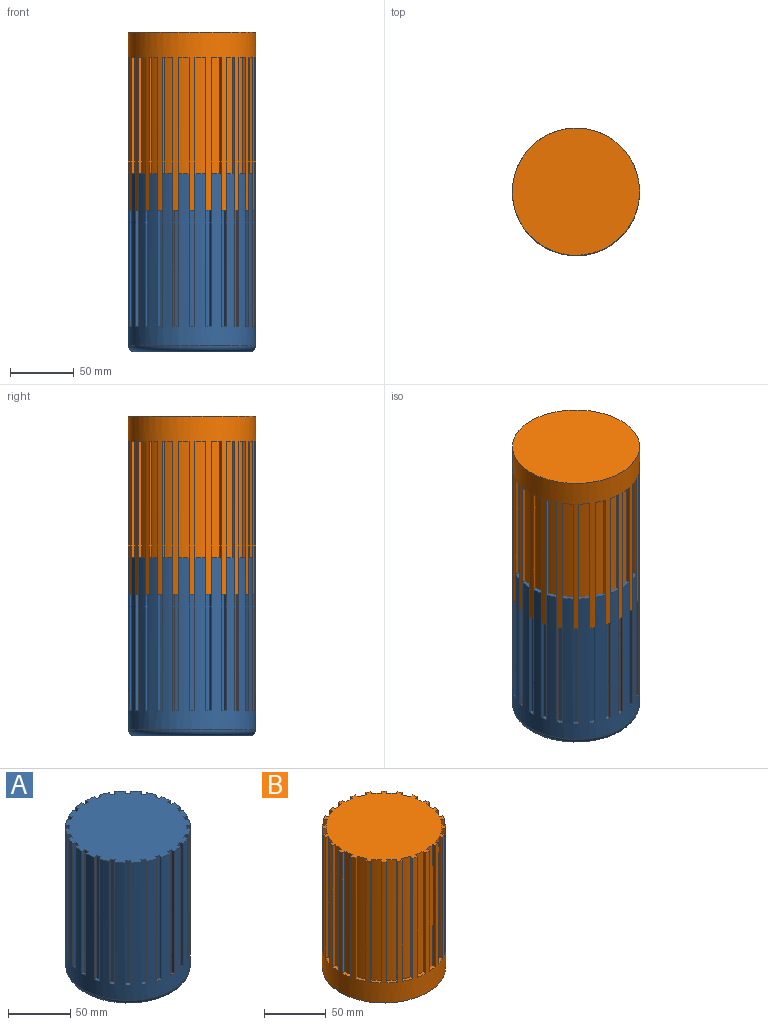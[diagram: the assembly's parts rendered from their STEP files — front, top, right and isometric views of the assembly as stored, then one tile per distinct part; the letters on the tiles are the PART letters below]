
ASSEMBLY  parts=2 mates=1
PART A: 102 faces, bbox 108.2x108.2x140 mm
  f0: plane 120x2.82mm, normal (0.94,0.34,0), area 360mm2, adj f1,f69,f70,f97
  f1: plane 120x3.86mm, normal (-0.26,0.97,0), area 480mm2, adj f0,f2,f70,f97
  f2: plane 120x2.95mm, normal (-0.98,-0.17,0), area 360mm2, adj f1,f69,f70,f97
  f3: plane 120x2.46mm, normal (0.82,0.57,0), area 360mm2, adj f4,f69,f70,f96
  f4: plane 120x3.46mm, normal (-0.5,0.87,0), area 480mm2, adj f3,f5,f70,f96
  f5: plane 120x2.72mm, normal (-0.91,-0.42,0), area 360mm2, adj f4,f69,f70,f96
  f6: plane 120x2.3mm, normal (0.64,0.77,0), area 360mm2, adj f7,f69,f70,f95
  f7: plane 120x2.83mm, normal (-0.71,0.71,0), area 480mm2, adj f6,f8,f70,f95
  f8: plane 120x2.3mm, normal (-0.77,-0.64,0), area 360mm2, adj f7,f69,f70,f95
  f9: plane 120x2.72mm, normal (0.42,0.91,0), area 360mm2, adj f10,f69,f70,f94
  f10: plane 120x3.46mm, normal (-0.87,0.5,0), area 480mm2, adj f9,f11,f70,f94
  f11: plane 120x2.46mm, normal (-0.57,-0.82,0), area 360mm2, adj f10,f69,f70,f94
  f12: plane 120x2.95mm, normal (0.17,0.98,0), area 360mm2, adj f13,f69,f70,f93
  f13: plane 120x3.86mm, normal (-0.97,0.26,0), area 480mm2, adj f12,f14,f70,f93
  f14: plane 120x2.82mm, normal (-0.34,-0.94,0), area 360mm2, adj f13,f69,f70,f93
  f15: plane 120x2.99mm, normal (-0.09,1,0), area 360mm2, adj f16,f69,f70,f92
  f16: plane 120x4mm, normal (-1,0,0), area 480mm2, adj f15,f17,f70,f92
  f17: plane 120x2.99mm, normal (-0.09,-1,0), area 360mm2, adj f16,f69,f70,f92
  f18: plane 120x2.82mm, normal (-0.34,0.94,0), area 360mm2, adj f19,f69,f70,f91
  f19: plane 120x3.86mm, normal (-0.97,-0.26,0), area 480mm2, adj f18,f20,f70,f91
  f20: plane 120x2.95mm, normal (0.17,-0.98,0), area 360mm2, adj f19,f69,f70,f91
  f21: plane 120x2.46mm, normal (-0.57,0.82,0), area 360mm2, adj f22,f69,f70,f90
  f22: plane 120x3.46mm, normal (-0.87,-0.5,0), area 480mm2, adj f21,f23,f70,f90
  f23: plane 120x2.72mm, normal (0.42,-0.91,0), area 360mm2, adj f22,f69,f70,f90
  f24: plane 120x2.3mm, normal (-0.77,0.64,0), area 360mm2, adj f25,f69,f70,f89
  f25: plane 120x2.83mm, normal (-0.71,-0.71,0), area 480mm2, adj f24,f26,f70,f89
  f26: plane 120x2.3mm, normal (0.64,-0.77,0), area 360mm2, adj f25,f69,f70,f89
  f27: plane 120x2.72mm, normal (-0.91,0.42,0), area 360mm2, adj f28,f69,f70,f88
  f28: plane 120x3.46mm, normal (-0.5,-0.87,0), area 480mm2, adj f27,f29,f70,f88
  f29: plane 120x2.46mm, normal (0.82,-0.57,0), area 360mm2, adj f28,f69,f70,f88
  f30: plane 120x2.95mm, normal (-0.98,0.17,0), area 360mm2, adj f31,f69,f70,f87
  f31: plane 120x3.86mm, normal (-0.26,-0.97,0), area 480mm2, adj f30,f32,f70,f87
  f32: plane 120x2.82mm, normal (0.94,-0.34,0), area 360mm2, adj f31,f69,f70,f87
  f33: plane 120x2.99mm, normal (-1,-0.09,0), area 360mm2, adj f34,f69,f70,f86
  f34: plane 120x4mm, normal (0,-1,0), area 480mm2, adj f33,f35,f70,f86
  f35: plane 120x2.99mm, normal (1,-0.09,0), area 360mm2, adj f34,f69,f70,f86
  f36: plane 120x2.82mm, normal (-0.94,-0.34,0), area 360mm2, adj f37,f69,f70,f85
  f37: plane 120x3.86mm, normal (0.26,-0.97,0), area 480mm2, adj f36,f38,f70,f85
  f38: plane 120x2.95mm, normal (0.98,0.17,0), area 360mm2, adj f37,f69,f70,f85
  f39: plane 120x2.46mm, normal (-0.82,-0.57,0), area 360mm2, adj f40,f69,f70,f84
  f40: plane 120x3.46mm, normal (0.5,-0.87,0), area 480mm2, adj f39,f41,f70,f84
  f41: plane 120x2.72mm, normal (0.91,0.42,0), area 360mm2, adj f40,f69,f70,f84
  f42: plane 120x2.3mm, normal (-0.64,-0.77,0), area 360mm2, adj f43,f69,f70,f83
  f43: plane 120x2.83mm, normal (0.71,-0.71,0), area 480mm2, adj f42,f44,f70,f83
  f44: plane 120x2.3mm, normal (0.77,0.64,0), area 360mm2, adj f43,f69,f70,f83
  f45: plane 120x2.72mm, normal (-0.42,-0.91,0), area 360mm2, adj f46,f69,f70,f82
  f46: plane 120x3.46mm, normal (0.87,-0.5,0), area 480mm2, adj f45,f47,f70,f82
  f47: plane 120x2.46mm, normal (0.57,0.82,0), area 360mm2, adj f46,f69,f70,f82
  f48: plane 120x2.95mm, normal (-0.17,-0.98,0), area 360mm2, adj f49,f69,f70,f81
  f49: plane 120x3.86mm, normal (0.97,-0.26,0), area 480mm2, adj f48,f50,f70,f81
  f50: plane 120x2.82mm, normal (0.34,0.94,0), area 360mm2, adj f49,f69,f70,f81
  f51: plane 120x2.99mm, normal (0.09,-1,0), area 360mm2, adj f52,f69,f70,f80
  f52: plane 120x4mm, normal (1,0,0), area 480mm2, adj f51,f53,f70,f80
  f53: plane 120x2.99mm, normal (0.09,1,0), area 360mm2, adj f52,f69,f70,f80
  f54: plane 120x2.82mm, normal (0.34,-0.94,0), area 360mm2, adj f55,f69,f70,f79
  f55: plane 120x3.86mm, normal (0.97,0.26,0), area 480mm2, adj f54,f56,f70,f79
  f56: plane 120x2.95mm, normal (-0.17,0.98,0), area 360mm2, adj f55,f69,f70,f79
  f57: plane 120x2.46mm, normal (0.57,-0.82,0), area 360mm2, adj f58,f69,f70,f78
  f58: plane 120x3.46mm, normal (0.87,0.5,0), area 480mm2, adj f57,f59,f70,f78
  f59: plane 120x2.72mm, normal (-0.42,0.91,0), area 360mm2, adj f58,f69,f70,f78
  f60: plane 120x2.3mm, normal (0.77,-0.64,0), area 360mm2, adj f61,f69,f70,f77
  f61: plane 120x2.83mm, normal (0.71,0.71,0), area 480mm2, adj f60,f62,f70,f77
  f62: plane 120x2.3mm, normal (-0.64,0.77,0), area 360mm2, adj f61,f69,f70,f77
  f63: plane 120x2.72mm, normal (0.91,-0.42,0), area 360mm2, adj f64,f69,f70,f76
  f64: plane 120x3.46mm, normal (0.5,0.87,0), area 480mm2, adj f63,f65,f70,f76
  f65: plane 120x2.46mm, normal (-0.82,0.57,0), area 360mm2, adj f64,f69,f70,f76
  f66: plane 120x2.95mm, normal (0.98,-0.17,0), area 360mm2, adj f67,f69,f70,f75
  f67: plane 120x3.86mm, normal (0.26,0.97,0), area 480mm2, adj f66,f68,f70,f75
  f68: plane 120x2.82mm, normal (-0.94,0.34,0), area 360mm2, adj f67,f69,f70,f75
  f69: cylinder r=50mm len=135mm, axis (0,0,-1), area 29313.1mm2, adj f0,f2,f3,f5,f6,f8,f9,f11
  f70: plane 99.9x99.9mm, normal (0,0,1), area 7544.6mm2, adj f0,f1,f2,f3,f4,f5,f6,f7
  f71: plane 120x4mm, normal (0,1,0), area 480mm2, adj f70,f72,f73,f74
  f72: plane 120x2.99mm, normal (-1,0.09,0), area 360mm2, adj f69,f70,f71,f74
  f73: plane 120x2.99mm, normal (1,0.09,0), area 360mm2, adj f69,f70,f71,f74
  f74: plane 4.52x3.04mm, normal (0,0,1), area 12.9mm2, adj f69,f71,f72,f73
  f75: plane 4.89x3.99mm, normal (0,0,1), area 12.9mm2, adj f66,f67,f68,f69
  f76: plane 5.19x4.72mm, normal (0,0,1), area 12.9mm2, adj f63,f64,f65,f69
  f77: plane 5.13x5.13mm, normal (0,0,1), area 12.9mm2, adj f60,f61,f62,f69
  f78: plane 5.19x4.72mm, normal (0,0,1), area 12.9mm2, adj f57,f58,f59,f69
  f79: plane 4.89x3.99mm, normal (0,0,1), area 12.9mm2, adj f54,f55,f56,f69
  f80: plane 4.52x3.06mm, normal (0,0,1), area 12.9mm2, adj f51,f52,f53,f98
  f81: plane 4.89x3.99mm, normal (0,0,1), area 12.9mm2, adj f48,f49,f50,f69
  f82: plane 5.19x4.72mm, normal (0,0,1), area 12.9mm2, adj f45,f46,f47,f69
  f83: plane 5.13x5.13mm, normal (0,0,1), area 12.9mm2, adj f42,f43,f44,f69
  f84: plane 5.19x4.72mm, normal (0,0,1), area 12.9mm2, adj f39,f40,f41,f69
  f85: plane 4.89x3.99mm, normal (0,0,1), area 12.9mm2, adj f36,f37,f38,f69
  f86: plane 4.52x3.04mm, normal (0,0,1), area 12.9mm2, adj f33,f34,f35,f69
  f87: plane 4.89x3.99mm, normal (0,0,1), area 12.9mm2, adj f30,f31,f32,f69
  f88: plane 5.19x4.72mm, normal (0,0,1), area 12.9mm2, adj f27,f28,f29,f69
  f89: plane 5.13x5.13mm, normal (0,0,1), area 12.9mm2, adj f24,f25,f26,f69
  f90: plane 5.19x4.72mm, normal (0,0,1), area 12.9mm2, adj f21,f22,f23,f69
  f91: plane 4.89x3.99mm, normal (0,0,1), area 12.9mm2, adj f18,f19,f20,f69
  f92: plane 4.52x3.04mm, normal (0,0,1), area 12.9mm2, adj f15,f16,f17,f69
  f93: plane 4.89x3.99mm, normal (0,0,1), area 12.9mm2, adj f12,f13,f14,f69
  f94: plane 5.19x4.72mm, normal (0,0,1), area 12.9mm2, adj f9,f10,f11,f69
  f95: plane 5.13x5.13mm, normal (0,0,1), area 12.9mm2, adj f6,f7,f8,f69
  f96: plane 5.19x4.72mm, normal (0,0,1), area 12.9mm2, adj f3,f4,f5,f69
  f97: plane 4.89x3.99mm, normal (0,0,1), area 12.9mm2, adj f0,f1,f2,f69
  f98: extruded ~15x4.52mm, area 67.9mm2, adj f69,f80,f101
  f99: plane 90x90mm, normal (0,0,-1), area 6361.7mm2, adj f100,f101
  f100: torus R=45mm, axis (0,0,-1), area 2343.5mm2, adj f69,f99,f101
  f101: bspline ~6.18x5.08mm, area 34.2mm2, adj f98,f99,f100
PART B: 99 faces, bbox 100x100x140 mm
  f0: plane 8.93x5.99mm, normal (0,0,1), area 25.3mm2, adj f24,f40,f43,f97
  f1: plane 8.51x7.51mm, normal (0,0,1), area 25.3mm2, adj f24,f42,f45,f96
  f2: plane 8.51x7.51mm, normal (0,0,1), area 25.3mm2, adj f24,f44,f47,f95
  f3: plane 8.93x5.99mm, normal (0,0,1), area 25.3mm2, adj f24,f46,f49,f94
  f4: plane 8.74x4.07mm, normal (0,0,1), area 25.3mm2, adj f24,f48,f51,f93
  f5: plane 8.74x4.07mm, normal (0,0,1), area 25.3mm2, adj f24,f50,f53,f92
  f6: plane 8.93x5.99mm, normal (0,0,1), area 25.3mm2, adj f24,f52,f55,f91
  f7: plane 8.51x7.51mm, normal (0,0,1), area 25.3mm2, adj f24,f54,f57,f90
  f8: plane 8.51x7.51mm, normal (0,0,1), area 25.3mm2, adj f24,f56,f59,f89
  f9: plane 8.93x5.99mm, normal (0,0,1), area 25.3mm2, adj f24,f58,f61,f88
  f10: plane 8.74x4.07mm, normal (0,0,1), area 25.3mm2, adj f24,f60,f63,f87
  f11: plane 8.74x4.07mm, normal (0,0,1), area 25.3mm2, adj f24,f62,f65,f86
  f12: plane 8.93x5.99mm, normal (0,0,1), area 25.3mm2, adj f24,f64,f67,f85
  f13: plane 8.51x7.51mm, normal (0,0,1), area 25.3mm2, adj f24,f66,f69,f84
  f14: plane 8.51x7.51mm, normal (0,0,1), area 25.3mm2, adj f24,f68,f71,f83
  f15: plane 8.93x5.99mm, normal (0,0,1), area 25.3mm2, adj f24,f70,f73,f82
  f16: plane 8.74x4.07mm, normal (0,0,1), area 25.3mm2, adj f24,f27,f72,f81
  f17: plane 8.74x4.07mm, normal (0,0,1), area 25.3mm2, adj f24,f26,f29,f80
  f18: plane 8.93x5.99mm, normal (0,0,1), area 25.3mm2, adj f24,f28,f31,f79
  f19: plane 8.51x7.51mm, normal (0,0,1), area 25.3mm2, adj f24,f30,f33,f78
  f20: plane 8.51x7.51mm, normal (0,0,1), area 25.3mm2, adj f24,f32,f35,f77
  f21: plane 8.93x5.99mm, normal (0,0,1), area 25.3mm2, adj f24,f34,f37,f76
  f22: plane 8.74x4.07mm, normal (0,0,1), area 25.3mm2, adj f24,f36,f39,f75
  f23: plane 8.74x4.07mm, normal (0,0,1), area 25.3mm2, adj f24,f38,f41,f74
  f24: cylinder r=50mm len=140mm, axis (0,0,-1), area 19313.7mm2, adj f0,f1,f2,f3,f4,f5,f6,f7
  f25: plane 100x100mm, normal (0,0,-1), area 7854mm2, adj f24
  f26: plane 120x2.99mm, normal (1,-0.09,0), area 360mm2, adj f17,f24,f80,f98
  f27: plane 120x2.99mm, normal (-1,-0.09,0), area 360mm2, adj f16,f24,f81,f98
  f28: plane 120x2.82mm, normal (0.94,-0.34,0), area 360mm2, adj f18,f24,f79,f98
  f29: plane 120x2.95mm, normal (-0.98,0.17,0), area 360mm2, adj f17,f24,f80,f98
  f30: plane 120x2.46mm, normal (0.82,-0.57,0), area 360mm2, adj f19,f24,f78,f98
  f31: plane 120x2.72mm, normal (-0.91,0.42,0), area 360mm2, adj f18,f24,f79,f98
  f32: plane 120x2.3mm, normal (0.64,-0.77,0), area 360mm2, adj f20,f24,f77,f98
  f33: plane 120x2.3mm, normal (-0.77,0.64,0), area 360mm2, adj f19,f24,f78,f98
  f34: plane 120x2.72mm, normal (0.42,-0.91,0), area 360mm2, adj f21,f24,f76,f98
  f35: plane 120x2.46mm, normal (-0.57,0.82,0), area 360mm2, adj f20,f24,f77,f98
  f36: plane 120x2.95mm, normal (0.17,-0.98,0), area 360mm2, adj f22,f24,f75,f98
  f37: plane 120x2.82mm, normal (-0.34,0.94,0), area 360mm2, adj f21,f24,f76,f98
  f38: plane 120x2.99mm, normal (-0.09,-1,0), area 360mm2, adj f23,f24,f74,f98
  f39: plane 120x2.99mm, normal (-0.09,1,0), area 360mm2, adj f22,f24,f75,f98
  f40: plane 120x2.82mm, normal (-0.34,-0.94,0), area 360mm2, adj f0,f24,f97,f98
  f41: plane 120x2.95mm, normal (0.17,0.98,0), area 360mm2, adj f23,f24,f74,f98
  f42: plane 120x2.46mm, normal (-0.57,-0.82,0), area 360mm2, adj f1,f24,f96,f98
  f43: plane 120x2.72mm, normal (0.42,0.91,0), area 360mm2, adj f0,f24,f97,f98
  f44: plane 120x2.3mm, normal (-0.77,-0.64,0), area 360mm2, adj f2,f24,f95,f98
  f45: plane 120x2.3mm, normal (0.64,0.77,0), area 360mm2, adj f1,f24,f96,f98
  f46: plane 120x2.72mm, normal (-0.91,-0.42,0), area 360mm2, adj f3,f24,f94,f98
  f47: plane 120x2.46mm, normal (0.82,0.57,0), area 360mm2, adj f2,f24,f95,f98
  f48: plane 120x2.95mm, normal (-0.98,-0.17,0), area 360mm2, adj f4,f24,f93,f98
  f49: plane 120x2.82mm, normal (0.94,0.34,0), area 360mm2, adj f3,f24,f94,f98
  f50: plane 120x2.99mm, normal (-1,0.09,0), area 360mm2, adj f5,f24,f92,f98
  f51: plane 120x2.99mm, normal (1,0.09,0), area 360mm2, adj f4,f24,f93,f98
  f52: plane 120x2.82mm, normal (-0.94,0.34,0), area 360mm2, adj f6,f24,f91,f98
  f53: plane 120x2.95mm, normal (0.98,-0.17,0), area 360mm2, adj f5,f24,f92,f98
  f54: plane 120x2.46mm, normal (-0.82,0.57,0), area 360mm2, adj f7,f24,f90,f98
  f55: plane 120x2.72mm, normal (0.91,-0.42,0), area 360mm2, adj f6,f24,f91,f98
  f56: plane 120x2.3mm, normal (-0.64,0.77,0), area 360mm2, adj f8,f24,f89,f98
  f57: plane 120x2.3mm, normal (0.77,-0.64,0), area 360mm2, adj f7,f24,f90,f98
  f58: plane 120x2.72mm, normal (-0.42,0.91,0), area 360mm2, adj f9,f24,f88,f98
  f59: plane 120x2.46mm, normal (0.57,-0.82,0), area 360mm2, adj f8,f24,f89,f98
  f60: plane 120x2.95mm, normal (-0.17,0.98,0), area 360mm2, adj f10,f24,f87,f98
  f61: plane 120x2.82mm, normal (0.34,-0.94,0), area 360mm2, adj f9,f24,f88,f98
  f62: plane 120x2.99mm, normal (0.09,1,0), area 360mm2, adj f11,f24,f86,f98
  f63: plane 120x2.99mm, normal (0.09,-1,0), area 360mm2, adj f10,f24,f87,f98
  f64: plane 120x2.82mm, normal (0.34,0.94,0), area 360mm2, adj f12,f24,f85,f98
  f65: plane 120x2.95mm, normal (-0.17,-0.98,0), area 360mm2, adj f11,f24,f86,f98
  f66: plane 120x2.46mm, normal (0.57,0.82,0), area 360mm2, adj f13,f24,f84,f98
  f67: plane 120x2.72mm, normal (-0.42,-0.91,0), area 360mm2, adj f12,f24,f85,f98
  f68: plane 120x2.3mm, normal (0.77,0.64,0), area 360mm2, adj f14,f24,f83,f98
  f69: plane 120x2.3mm, normal (-0.64,-0.77,0), area 360mm2, adj f13,f24,f84,f98
  f70: plane 120x2.72mm, normal (0.91,0.42,0), area 360mm2, adj f15,f24,f82,f98
  f71: plane 120x2.46mm, normal (-0.82,-0.57,0), area 360mm2, adj f14,f24,f83,f98
  f72: plane 120x2.95mm, normal (0.98,0.17,0), area 360mm2, adj f16,f24,f81,f98
  f73: plane 120x2.82mm, normal (-0.94,-0.34,0), area 360mm2, adj f15,f24,f82,f98
  f74: cylinder r=47mm len=120mm, axis (0,0,-1), area 996.5mm2, adj f23,f38,f41,f98
  f75: cylinder r=47mm len=120mm, axis (0,0,-1), area 996.5mm2, adj f22,f36,f39,f98
  f76: cylinder r=47mm len=120mm, axis (0,0,-1), area 996.5mm2, adj f21,f34,f37,f98
  f77: cylinder r=47mm len=120mm, axis (0,0,-1), area 996.5mm2, adj f20,f32,f35,f98
  f78: cylinder r=47mm len=120mm, axis (0,0,-1), area 996.5mm2, adj f19,f30,f33,f98
  f79: cylinder r=47mm len=120mm, axis (0,0,-1), area 996.5mm2, adj f18,f28,f31,f98
  f80: cylinder r=47mm len=120mm, axis (0,0,-1), area 996.5mm2, adj f17,f26,f29,f98
  f81: cylinder r=47mm len=120mm, axis (0,0,-1), area 996.5mm2, adj f16,f27,f72,f98
  f82: cylinder r=47mm len=120mm, axis (0,0,-1), area 996.5mm2, adj f15,f70,f73,f98
  f83: cylinder r=47mm len=120mm, axis (0,0,-1), area 996.5mm2, adj f14,f68,f71,f98
  f84: cylinder r=47mm len=120mm, axis (0,0,-1), area 996.5mm2, adj f13,f66,f69,f98
  f85: cylinder r=47mm len=120mm, axis (0,0,-1), area 996.5mm2, adj f12,f64,f67,f98
  f86: cylinder r=47mm len=120mm, axis (0,0,-1), area 996.5mm2, adj f11,f62,f65,f98
  f87: cylinder r=47mm len=120mm, axis (0,0,-1), area 996.5mm2, adj f10,f60,f63,f98
  f88: cylinder r=47mm len=120mm, axis (0,0,-1), area 996.5mm2, adj f9,f58,f61,f98
  f89: cylinder r=47mm len=120mm, axis (0,0,-1), area 996.5mm2, adj f8,f56,f59,f98
  f90: cylinder r=47mm len=120mm, axis (0,0,-1), area 996.5mm2, adj f7,f54,f57,f98
  f91: cylinder r=47mm len=120mm, axis (0,0,-1), area 996.5mm2, adj f6,f52,f55,f98
  f92: cylinder r=47mm len=120mm, axis (0,0,-1), area 996.5mm2, adj f5,f50,f53,f98
  f93: cylinder r=47mm len=120mm, axis (0,0,-1), area 996.5mm2, adj f4,f48,f51,f98
  f94: cylinder r=47mm len=120mm, axis (0,0,-1), area 996.5mm2, adj f3,f46,f49,f98
  f95: cylinder r=47mm len=120mm, axis (0,0,-1), area 996.5mm2, adj f2,f44,f47,f98
  f96: cylinder r=47mm len=120mm, axis (0,0,-1), area 996.5mm2, adj f1,f42,f45,f98
  f97: cylinder r=47mm len=120mm, axis (0,0,-1), area 996.5mm2, adj f0,f40,f43,f98
  f98: plane 100x100mm, normal (0,0,1), area 7247.2mm2, adj f24,f26,f27,f28,f29,f30,f31,f32
PLACE A t=(75.15,142.28,116.8)mm
PLACE B rot(axis=(0,1,0),180deg) t=(75.15,142.28,348.17)mm fixed
MATE slider A.f86 <-> B.f98  axis (0,0,1) through (73.02,93.82,116.8)mm
